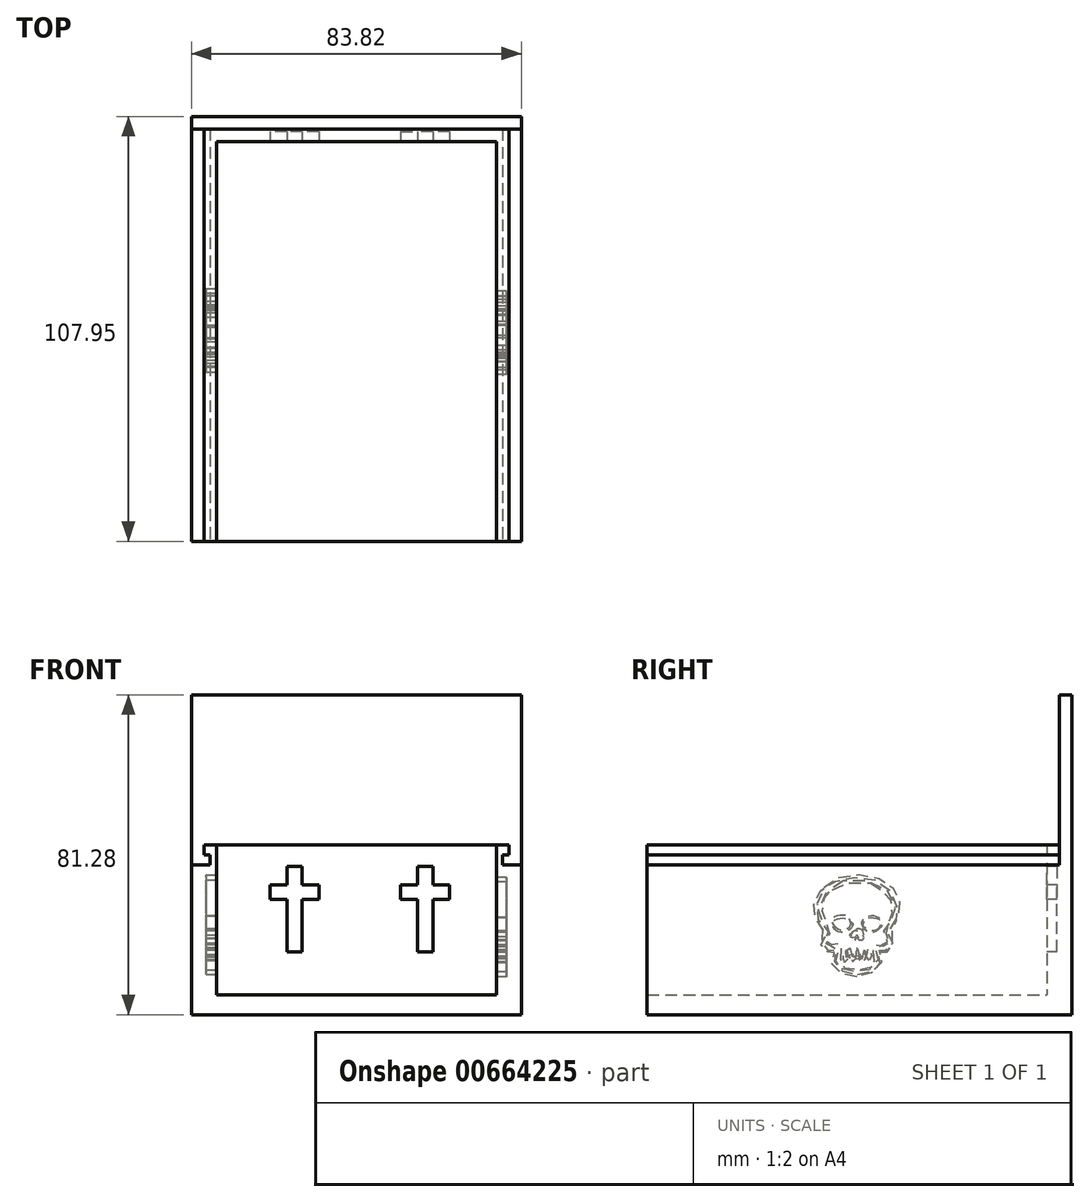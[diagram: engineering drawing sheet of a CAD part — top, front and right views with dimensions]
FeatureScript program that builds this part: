
annotation { "Feature Type Name" : "Feature", "Feature Type Description" : "" }
export const myFeature = defineFeature(function(context is Context, id is Id, definition is map)
    precondition{}
    {
        {
            var Q0;
            Q0=qCreatedBy(makeId("Top.planeOp"),FACE);
            var sketch = newSketch(context, id + "F0", { "sketchPlane" : qUnion([Q0])});
            skLineSegment(sketch, "E0.bottom", {"start": v(-35.56, 48.26) * mm, "end": v(35.56, 48.26) * mm});
            skLineSegment(sketch, "E0.top", {"start": v(-35.56, -48.26) * mm, "end": v(35.56, -48.26) * mm});
            skLineSegment(sketch, "E0.left", {"start": v(-35.56, 48.26) * mm, "end": v(-35.56, -48.26) * mm});
            skLineSegment(sketch, "E0.right", {"start": v(35.56, 48.26) * mm, "end": v(35.56, -48.26) * mm});
            skPoint(sketch, "E0.middle", {"position": v(0, 0) * mm});
            skLineSegment(sketch, "E1.bottom", {"start": v(-38.73, 51.44) * mm, "end": v(38.74, 51.44) * mm});
            skLineSegment(sketch, "E1.top", {"start": v(-38.74, -51.43) * mm, "end": v(38.73, -51.43) * mm});
            skLineSegment(sketch, "E1.left", {"start": v(-38.73, 51.44) * mm, "end": v(-38.74, -51.44) * mm});
            skLineSegment(sketch, "E1.right", {"start": v(38.74, 51.44) * mm, "end": v(38.73, -51.44) * mm});
            skLineSegment(sketch, "E2.bottom", {"start": v(-41.91, 54.61) * mm, "end": v(41.91, 54.61) * mm});
            skLineSegment(sketch, "E2.top", {"start": v(-41.91, -54.6) * mm, "end": v(41.91, -54.6) * mm});
            skLineSegment(sketch, "E2.left", {"start": v(-41.91, 54.61) * mm, "end": v(-41.91, -54.61) * mm});
            skLineSegment(sketch, "E2.right", {"start": v(41.91, 54.61) * mm, "end": v(41.91, -54.61) * mm});
            skLineSegment(sketch, "E3", {"start": v(-35.56, -48.26) * mm, "end": v(-41.91, -48.26) * mm});
            skLineSegment(sketch, "E4", {"start": v(35.56, -48.26) * mm, "end": v(41.91, -48.26) * mm});
            skSolve(sketch);
        }
        {
            var Q0;
            Q0=makeQuery(id+"F0.imprint","IMPRINT",FACE,{"disambiguationData":[TD([[makeQuery(id+"F0.imprint","IMPRINT",EDGE,{"derivedFrom":sQuery(id+"F0.wireOp",EDGE,"E1.bottom")}),1.0]])]});
            extrude(context, id + "F1", {"entities" : qUnion([Q0]), "depth" : 45.72 * mm, "offsetDistance" : 25.4 * mm});
        }
        {
            var Q0;
            Q0=makeQuery(id+"F0.imprint","IMPRINT",FACE,{"disambiguationData":[TD([[makeQuery(id+"F0.imprint","IMPRINT",EDGE,{"derivedFrom":sQuery(id+"F0.wireOp",EDGE,"E0.bottom")}),-1.0]])]});
            var Q1;
            Q1=makeQuery(id+"F0.imprint","IMPRINT",FACE,{"disambiguationData":[TD([[makeQuery(id+"F0.imprint","IMPRINT",EDGE,{"derivedFrom":sQuery(id+"F0.wireOp",EDGE,"E0.bottom")}),1.0]])]});
            extrude(context, id + "F2", {"entities" : qUnion([Q0, Q1]), "operationType" : NewBodyOperationType.ADD, "depth" : 12.7 * mm, "offsetDistance" : 25.4 * mm});
        }
        {
            var Q0;
            Q0=makeQuery(id+"F0.imprint","IMPRINT",FACE,{"disambiguationData":[TD([[makeQuery(id+"F0.imprint","IMPRINT",EDGE,{"derivedFrom":sQuery(id+"F0.wireOp",EDGE,"E0.bottom")}),1.0]])]});
            extrude(context, id + "F3", {"entities" : qUnion([Q0]), "operationType" : NewBodyOperationType.ADD, "depth" : 50.8 * mm, "offsetDistance" : 25.4 * mm});
        }
        {
            var Q0;
            Q0=makeQuery(id+"F3.opExtrude","SWEPT_FACE",FACE,{"disambiguationData":[OSD([sQuery(id+"F0.wireOp",EDGE,"E0.bottom")])]});
            var sketch = newSketch(context, id + "F4", { "sketchPlane" : qUnion([Q0])});
            skLineSegment(sketch, "E5", {"start": v(-21.92, 40.58) * mm, "end": v(-9.48, 40.58) * mm});
            skLineSegment(sketch, "E6", {"start": v(-9.48, 40.58) * mm, "end": v(-9.48, 36.95) * mm});
            skLineSegment(sketch, "E7", {"start": v(-9.48, 36.95) * mm, "end": v(-21.92, 36.95) * mm});
            skLineSegment(sketch, "E8", {"start": v(-21.92, 36.95) * mm, "end": v(-21.92, 40.58) * mm});
            skLineSegment(sketch, "E9", {"start": v(-15.7, 36.95) * mm, "end": v(-15.7, 24.23) * mm});
            skLineSegment(sketch, "E10", {"start": v(-15.7, 45.25) * mm, "end": v(-17.6, 45.25) * mm});
            skLineSegment(sketch, "E11", {"start": v(-17.6, 45.25) * mm, "end": v(-13.73, 45.25) * mm});
            skLineSegment(sketch, "E12", {"start": v(-13.73, 45.25) * mm, "end": v(-13.73, 23.57) * mm});
            skLineSegment(sketch, "E13", {"start": v(-13.73, 23.57) * mm, "end": v(-17.6, 23.57) * mm});
            skLineSegment(sketch, "E14", {"start": v(-17.6, 23.57) * mm, "end": v(-17.6, 45.25) * mm});
            skLineSegment(sketch, "E15", {"start": v(11.25, 40.6) * mm, "end": v(23.7, 40.6) * mm});
            skLineSegment(sketch, "E16", {"start": v(23.7, 40.6) * mm, "end": v(23.7, 36.97) * mm});
            skLineSegment(sketch, "E17", {"start": v(23.7, 36.97) * mm, "end": v(11.25, 36.97) * mm});
            skLineSegment(sketch, "E18", {"start": v(11.25, 36.97) * mm, "end": v(11.25, 40.6) * mm});
            skLineSegment(sketch, "E19", {"start": v(15.58, 45.26) * mm, "end": v(19.44, 45.26) * mm});
            skLineSegment(sketch, "E20", {"start": v(19.44, 45.26) * mm, "end": v(19.44, 23.59) * mm});
            skLineSegment(sketch, "E21", {"start": v(19.44, 23.59) * mm, "end": v(15.58, 23.59) * mm});
            skLineSegment(sketch, "E22", {"start": v(15.58, 23.59) * mm, "end": v(15.58, 45.26) * mm});
            skSolve(sketch);
        }
        {
            var Q0;
            Q0 = qSketchRegion(id + "F4", true);
            extrude(context, id + "F5", {"entities" : qUnion([Q0]), "operationType" : NewBodyOperationType.REMOVE, "oppositeDirection" : true, "depth" : 2.54 * mm, "offsetDistance" : 25.4 * mm});
        }
        {
            var Q0;
            Q0=makeQuery(id+"F3.opExtrude","SWEPT_FACE",FACE,{"disambiguationData":[OSD([sQuery(id+"F0.wireOp",EDGE,"E0.left")])]});
            var sketch = newSketch(context, id + "F6", { "sketchPlane" : qUnion([Q0])});
            skFitSpline(sketch, "E23", {"points": [v(-3.48, 41.6) * mm, v(-6.98, 39.1) * mm, v(-8.94, 36.07) * mm, v(-8.17, 31.6) * mm, v(-7.36, 29.82) * mm, v(-7.6, 27.83) * mm, v(-8.05, 26.07) * mm, v(-6.59, 25.46) * mm, v(-5.74, 25.8) * mm, v(-4.17, 25.42) * mm, v(-4.08, 24.6) * mm, v(-4.26, 22.37) * mm, v(-3.84, 20.01) * mm, v(0.07, 19.06) * mm, v(4.06, 20) * mm, v(5.35, 21.75) * mm, v(4.77, 24.34) * mm, v(6.05, 25.5) * mm, v(7.42, 25.48) * mm, v(7.65, 26.53) * mm, v(6.85, 29.25) * mm, v(9.08, 31.8) * mm, v(7.97, 38.98) * mm, v(-3.48, 41.6) * mm]});
            skFitSpline(sketch, "E24", {"points": [v(-1.81, 24.6) * mm, v(-1.36, 22.37) * mm, v(-0.58, 24.16) * mm, v(-0.04, 24.6) * mm, v(0.17, 23.93) * mm, v(0.54, 22.37) * mm, v(1.28, 24.13) * mm, v(2.4, 22.37) * mm, v(2.88, 24.6) * mm, v(3.56, 22.91) * mm, v(2.96, 21.49) * mm, v(1.62, 23) * mm, v(1.02, 21.62) * mm, v(-0.16, 22.82) * mm, v(-1.1, 21.45) * mm, v(-2.57, 23.8) * mm, v(-1.81, 24.6) * mm]});
            skFitSpline(sketch, "E25", {"points": [v(-2.96, 32.8) * mm, v(-6.4, 31.85) * mm, v(-4.26, 29.17) * mm, v(-1.81, 30.11) * mm, v(-1.81, 31.7) * mm, v(-2.96, 32.8) * mm]});
            skFitSpline(sketch, "E26", {"points": [v(1.64, 31.89) * mm, v(1.1, 30.65) * mm, v(3.98, 29.03) * mm, v(5.86, 30.16) * mm, v(5.89, 31.9) * mm, v(3.37, 32.7) * mm, v(1.64, 31.89) * mm]});
            skFitSpline(sketch, "E27", {"points": [v(-0.04, 27.93) * mm, v(-0.58, 27.28) * mm, v(-1.81, 27.7) * mm, v(0.54, 29.52) * mm, v(1.5, 27.57) * mm, v(0.54, 27.08) * mm, v(-0.04, 27.93) * mm]});
            skPoint(sketch, "E28.18.internal.snap0", {"position": v(-8.94, 30.33) * mm});
            skFitSpline(sketch, "E28", {"points": [v(0.07, 17.85) * mm, v(4.62, 19.06) * mm, v(6.3, 21.62) * mm, v(5.67, 23.93) * mm, v(6.14, 24.16) * mm, v(7.54, 24.16) * mm, v(9.08, 25.48) * mm, v(8.3, 27.85) * mm, v(7.65, 28.63) * mm, v(9.08, 30.33) * mm, v(10.57, 33.02) * mm, v(10.74, 36.88) * mm, v(7.97, 40.84) * mm, v(1.02, 43.07) * mm, v(-6.4, 41.6) * mm, v(-9.91, 36.93) * mm, v(-9.9, 31.85) * mm, v(-8.94, 30.33) * mm, v(-8.94, 26.53) * mm, v(-8.15, 24.16) * mm, v(-6.4, 24.16) * mm, v(-5.28, 23.93) * mm, v(-5.8, 21.62) * mm, v(-4.26, 19.06) * mm, v(0.07, 17.85) * mm]});
            skPoint(sketch, "E29.18.internal.snap0", {"position": v(-5.14, 42.6) * mm});
            skSolve(sketch);
        }
        {
            var Q0;
            Q0 = qSketchRegion(id + "F6", true);
            var Q1;
            Q1=makeQuery(id+"F6.imprint","IMPRINT",FACE,{"disambiguationData":[TD([[makeQuery(id+"F6.imprint","IMPRINT",EDGE,{"derivedFrom":sQuery(id+"F6.wireOp",EDGE,"E25")}),1.0]])]});
            var Q2;
            Q2=makeQuery(id+"F6.imprint","IMPRINT",FACE,{"disambiguationData":[TD([[makeQuery(id+"F6.imprint","IMPRINT",EDGE,{"derivedFrom":sQuery(id+"F6.wireOp",EDGE,"E27")}),-1.0]])]});
            var Q3;
            Q3=makeQuery(id+"F6.imprint","IMPRINT",FACE,{"disambiguationData":[TD([[makeQuery(id+"F6.imprint","IMPRINT",EDGE,{"derivedFrom":sQuery(id+"F6.wireOp",EDGE,"E26")}),1.0]])]});
            var Q4;
            Q4=makeQuery(id+"F6.imprint","IMPRINT",FACE,{"disambiguationData":[TD([[makeQuery(id+"F6.imprint","IMPRINT",EDGE,{"derivedFrom":sQuery(id+"F6.wireOp",EDGE,"E24")}),-1.0]])]});
            extrude(context, id + "F7", {"entities" : qUnion([Q0, Q1, Q2, Q3, Q4]), "operationType" : NewBodyOperationType.REMOVE, "oppositeDirection" : true, "depth" : 2.54 * mm, "offsetDistance" : 25.4 * mm});
        }
        {
            var Q0;
            Q0=makeQuery(id+"F3.opExtrude","SWEPT_FACE",FACE,{"disambiguationData":[OSD([sQuery(id+"F0.wireOp",EDGE,"E1.left")])]});
            var sketch = newSketch(context, id + "F8", { "sketchPlane" : qUnion([Q0])});
            skLineSegment(sketch, "E30.bottom", {"start": v(-51.43, 45.72) * mm, "end": v(48.26, 45.72) * mm});
            skLineSegment(sketch, "E30.top", {"start": v(-51.43, 48.26) * mm, "end": v(48.26, 48.26) * mm});
            skLineSegment(sketch, "E30.left", {"start": v(-51.43, 45.72) * mm, "end": v(-51.43, 48.26) * mm});
            skLineSegment(sketch, "E30.right", {"start": v(48.26, 45.72) * mm, "end": v(48.26, 48.26) * mm});
            skSolve(sketch);
        }
        {
            var Q0;
            Q0 = qSketchRegion(id + "F8", true);
            extrude(context, id + "F9", {"entities" : qUnion([Q0]), "operationType" : NewBodyOperationType.REMOVE, "depth" : -1.57 * mm, "offsetDistance" : 25.4 * mm});
        }
        {
            var Q0;
            Q0=makeQuery(id+"F3.opExtrude","SWEPT_FACE",FACE,{"disambiguationData":[OSD([sQuery(id+"F0.wireOp",EDGE,"E1.right")])]});
            var sketch = newSketch(context, id + "F10", { "sketchPlane" : qUnion([Q0])});
            skLineSegment(sketch, "E31.bottom", {"start": v(-48.26, 45.72) * mm, "end": v(51.44, 45.72) * mm});
            skLineSegment(sketch, "E31.top", {"start": v(-48.26, 48.26) * mm, "end": v(51.44, 48.26) * mm});
            skLineSegment(sketch, "E31.left", {"start": v(-48.26, 45.72) * mm, "end": v(-48.26, 48.26) * mm});
            skLineSegment(sketch, "E31.right", {"start": v(51.44, 45.72) * mm, "end": v(51.44, 48.26) * mm});
            skSolve(sketch);
        }
        {
            var Q0;
            Q0 = qSketchRegion(id + "F10", true);
            extrude(context, id + "F11", {"entities" : qUnion([Q0]), "operationType" : NewBodyOperationType.REMOVE, "depth" : -1.57 * mm, "offsetDistance" : 25.4 * mm});
        }
        {
            var Q0;
            {var subQ0=sQuery(id+"F0.wireOp",EDGE,"E4");var subQ1=sQuery(id+"F0.wireOp",EDGE,"E3");var subQ2=sQuery(id+"F0.wireOp",EDGE,"E1.right");var subQ3=sQuery(id+"F0.wireOp",EDGE,"E1.left");var subQ4=sQuery(id+"F0.wireOp",EDGE,"E1.bottom");Q0=makeQuery(id+"F2.boolean.opBoolean","MERGE",FACE,{"derivedFrom":[makeQuery(id+"F1.opExtrude","CAP_FACE",FACE,{"disambiguationData":[OSD([subQ4,subQ3,subQ2,sQuery(id+"F0.wireOp",EDGE,"E2.bottom"),sQuery(id+"F0.wireOp",EDGE,"E2.left"),sQuery(id+"F0.wireOp",EDGE,"E2.right"),subQ1,subQ0])],"isStart":true}),makeQuery(id+"F2.opExtrude","CAP_FACE",FACE,{"disambiguationData":[OSD([sQuery(id+"F0.wireOp",EDGE,"E0.top"),subQ4,subQ3,subQ2,subQ1,subQ0])],"isStart":true})]});}
            var sketch = newSketch(context, id + "F12", { "sketchPlane" : qUnion([Q0])});
            skLineSegment(sketch, "E32.bottom", {"start": v(-41.91, 48.26) * mm, "end": v(41.91, 48.26) * mm});
            skLineSegment(sketch, "E32.top", {"start": v(-41.91, -54.61) * mm, "end": v(41.91, -54.61) * mm});
            skLineSegment(sketch, "E32.left", {"start": v(-41.91, 48.26) * mm, "end": v(-41.91, -54.61) * mm});
            skLineSegment(sketch, "E32.right", {"start": v(41.91, 48.26) * mm, "end": v(41.91, -54.61) * mm});
            skSolve(sketch);
        }
        {
            var Q0;
            Q0 = qSketchRegion(id + "F12", true);
            extrude(context, id + "F13", {"entities" : qUnion([Q0]), "operationType" : NewBodyOperationType.REMOVE, "oppositeDirection" : true, "depth" : 7.62 * mm, "offsetDistance" : 25.4 * mm});
        }
        {
            var Q0;
            Q0=makeQuery(id+"F11.boolean.opBoolean","MERGE",FACE,{"derivedFrom":[makeQuery(id+"F9.boolean.opBoolean","MERGE",FACE,{"derivedFrom":[makeQuery(id+"F1.opExtrude","CAP_FACE",FACE,{"disambiguationData":[OSD([sQuery(id+"F0.wireOp",EDGE,"E1.bottom"),sQuery(id+"F0.wireOp",EDGE,"E1.left"),sQuery(id+"F0.wireOp",EDGE,"E1.right"),sQuery(id+"F0.wireOp",EDGE,"E2.bottom"),sQuery(id+"F0.wireOp",EDGE,"E2.left"),sQuery(id+"F0.wireOp",EDGE,"E2.right"),sQuery(id+"F0.wireOp",EDGE,"E3"),sQuery(id+"F0.wireOp",EDGE,"E4")])],"isStart":false}),makeQuery(id+"F9.opExtrude","SWEPT_FACE",FACE,{"disambiguationData":[OSD([sQuery(id+"F8.wireOp",EDGE,"E30.bottom")])]})]}),makeQuery(id+"F11.opExtrude","SWEPT_FACE",FACE,{"disambiguationData":[OSD([sQuery(id+"F10.wireOp",EDGE,"E31.bottom")])]})]});
            var sketch = newSketch(context, id + "F14", { "sketchPlane" : qUnion([Q0])});
            skLineSegment(sketch, "E33.bottom", {"start": v(-41.91, 54.61) * mm, "end": v(41.91, 54.61) * mm});
            skLineSegment(sketch, "E33.top", {"start": v(-41.91, 51.44) * mm, "end": v(41.91, 51.44) * mm});
            skLineSegment(sketch, "E33.left", {"start": v(-41.91, 54.61) * mm, "end": v(-41.91, 51.44) * mm});
            skLineSegment(sketch, "E33.right", {"start": v(41.91, 54.61) * mm, "end": v(41.91, 51.44) * mm});
            skSolve(sketch);
        }
        {
            var Q0;
            Q0 = qSketchRegion(id + "F14", true);
            extrude(context, id + "F15", {"entities" : qUnion([Q0]), "operationType" : NewBodyOperationType.ADD, "depth" : 43.18 * mm, "offsetDistance" : 25.4 * mm});
        }
        {
            var Q0;
            Q0=makeQuery(id+"F3.opExtrude","SWEPT_FACE",FACE,{"disambiguationData":[OSD([sQuery(id+"F0.wireOp",EDGE,"E0.right")])]});
            var sketch = newSketch(context, id + "F16", { "sketchPlane" : qUnion([Q0])});
            skFitSpline(sketch, "E34", {"points": [v(-3.42, 41.06) * mm, v(-6.93, 38.57) * mm, v(-8.89, 35.54) * mm, v(-8.11, 31.06) * mm, v(-7.3, 29.29) * mm, v(-7.55, 27.3) * mm, v(-8, 25.54) * mm, v(-6.54, 24.93) * mm, v(-5.69, 25.27) * mm, v(-4.11, 24.9) * mm, v(-4.02, 24.07) * mm, v(-4.2, 21.84) * mm, v(-3.79, 19.48) * mm, v(0.12, 18.53) * mm, v(4.11, 19.47) * mm, v(5.4, 21.22) * mm, v(4.82, 23.81) * mm, v(6.1, 24.97) * mm, v(7.47, 24.94) * mm, v(7.7, 26) * mm, v(6.9, 28.71) * mm, v(9.13, 31.27) * mm, v(8.02, 38.45) * mm, v(-3.42, 41.06) * mm]});
            skFitSpline(sketch, "E35", {"points": [v(-1.7, 24.07) * mm, v(-1.25, 21.84) * mm, v(-0.47, 23.57) * mm, v(0.06, 24.07) * mm, v(0.27, 23.33) * mm, v(0.65, 21.84) * mm, v(1.4, 23.54) * mm, v(2.51, 21.84) * mm, v(3, 24.07) * mm, v(3.67, 22.32) * mm, v(3.07, 20.9) * mm, v(1.73, 22.4) * mm, v(1.13, 21.02) * mm, v(-0.05, 22.23) * mm, v(-1, 20.86) * mm, v(-2.47, 23.2) * mm, v(-1.7, 24.07) * mm]});
            skFitSpline(sketch, "E36", {"points": [v(-2.85, 32.2) * mm, v(-6.3, 31.25) * mm, v(-4.2, 28.57) * mm, v(-1.7, 29.51) * mm, v(-1.7, 31.1) * mm, v(-2.85, 32.2) * mm]});
            skFitSpline(sketch, "E37", {"points": [v(1.7, 31.36) * mm, v(1.15, 30.12) * mm, v(4.03, 28.5) * mm, v(5.9, 29.63) * mm, v(5.94, 31.37) * mm, v(3.42, 32.16) * mm, v(1.7, 31.36) * mm]});
            skFitSpline(sketch, "E38", {"points": [v(0.06, 27.33) * mm, v(-0.47, 26.68) * mm, v(-1.7, 27.1) * mm, v(0.65, 28.93) * mm, v(1.6, 26.97) * mm, v(0.65, 26.48) * mm, v(0.06, 27.33) * mm]});
            skPoint(sketch, "E39.18.internal.snap0", {"position": v(-8.89, 29.8) * mm});
            skFitSpline(sketch, "E39", {"points": [v(0.12, 17.25) * mm, v(4.73, 18.53) * mm, v(6.4, 21.02) * mm, v(5.77, 23.33) * mm, v(6.25, 23.57) * mm, v(7.65, 23.57) * mm, v(9.13, 24.94) * mm, v(8.4, 27.25) * mm, v(7.7, 28.03) * mm, v(9.13, 29.8) * mm, v(10.68, 32.42) * mm, v(10.85, 36.29) * mm, v(8.02, 40.24) * mm, v(1.13, 42.47) * mm, v(-6.3, 41.06) * mm, v(-9.8, 36.33) * mm, v(-9.8, 31.25) * mm, v(-8.89, 29.8) * mm, v(-8.89, 26) * mm, v(-8.04, 23.57) * mm, v(-6.3, 23.57) * mm, v(-5.17, 23.33) * mm, v(-5.69, 21.02) * mm, v(-4.2, 18.53) * mm, v(0.12, 17.25) * mm]});
            skSolve(sketch);
        }
        {
            var Q0;
            Q0=makeQuery(id+"F16.imprint","IMPRINT",FACE,{"disambiguationData":[TD([[makeQuery(id+"F16.imprint","IMPRINT",EDGE,{"derivedFrom":sQuery(id+"F16.wireOp",EDGE,"E36")}),1.0]])]});
            var Q1;
            Q1=makeQuery(id+"F16.imprint","IMPRINT",FACE,{"disambiguationData":[TD([[makeQuery(id+"F16.imprint","IMPRINT",EDGE,{"derivedFrom":sQuery(id+"F16.wireOp",EDGE,"E37")}),1.0]])]});
            var Q2;
            Q2=makeQuery(id+"F16.imprint","IMPRINT",FACE,{"disambiguationData":[TD([[makeQuery(id+"F16.imprint","IMPRINT",EDGE,{"derivedFrom":sQuery(id+"F16.wireOp",EDGE,"E35")}),-1.0]])]});
            var Q3;
            Q3=makeQuery(id+"F16.imprint","IMPRINT",FACE,{"disambiguationData":[TD([[makeQuery(id+"F16.imprint","IMPRINT",EDGE,{"derivedFrom":sQuery(id+"F16.wireOp",EDGE,"E38")}),-1.0]])]});
            var Q4;
            Q4=makeQuery(id+"F16.imprint","IMPRINT",FACE,{"disambiguationData":[TD([[makeQuery(id+"F16.imprint","IMPRINT",EDGE,{"derivedFrom":sQuery(id+"F16.wireOp",EDGE,"E34")}),-1.0]])]});
            extrude(context, id + "F17", {"entities" : qUnion([Q0, Q1, Q2, Q3, Q4]), "operationType" : NewBodyOperationType.REMOVE, "oppositeDirection" : true, "depth" : 2.54 * mm, "offsetDistance" : 25.4 * mm});
        }
        {
            var Q0;
            {var subQ0=sQuery(id+"F0.wireOp",EDGE,"E4");var subQ1=sQuery(id+"F0.wireOp",EDGE,"E3");Q0=makeQuery(id+"F3.boolean.opBoolean","MERGE",FACE,{"derivedFrom":[makeQuery(id+"F2.boolean.opBoolean","MERGE",FACE,{"derivedFrom":[makeQuery(id+"F1.opExtrude","SWEPT_FACE",FACE,{"disambiguationData":[OSD([subQ1])]}),makeQuery(id+"F1.opExtrude","SWEPT_FACE",FACE,{"disambiguationData":[OSD([subQ0])]}),makeQuery(id+"F2.opExtrude","SWEPT_FACE",FACE,{"disambiguationData":[OSD([sQuery(id+"F0.wireOp",EDGE,"E0.top"),subQ1,subQ0])]})]}),makeQuery(id+"F3.opExtrude","SWEPT_FACE",FACE,{"disambiguationData":[OSD([subQ1])]}),makeQuery(id+"F3.opExtrude","SWEPT_FACE",FACE,{"disambiguationData":[OSD([subQ0])]})]});}
            var sketch = newSketch(context, id + "F18", { "sketchPlane" : qUnion([Q0])});
            skLineSegment(sketch, "E40", {"start": v(-38.74, 50.8) * mm, "end": v(-35.56, 50.8) * mm});
            skLineSegment(sketch, "E41", {"start": v(-35.56, 50.8) * mm, "end": v(-35.56, 12.7) * mm});
            skLineSegment(sketch, "E42", {"start": v(-35.56, 12.7) * mm, "end": v(35.56, 12.7) * mm});
            skLineSegment(sketch, "E43", {"start": v(35.56, 12.7) * mm, "end": v(35.56, 50.8) * mm});
            skLineSegment(sketch, "E44", {"start": v(35.56, 50.8) * mm, "end": v(38.74, 50.8) * mm});
            skLineSegment(sketch, "E45", {"start": v(38.74, 50.8) * mm, "end": v(38.74, 48.26) * mm});
            skLineSegment(sketch, "E46", {"start": v(38.74, 48.26) * mm, "end": v(37.16, 48.26) * mm});
            skLineSegment(sketch, "E47", {"start": v(37.16, 48.26) * mm, "end": v(37.16, 45.72) * mm});
            skLineSegment(sketch, "E48", {"start": v(37.16, 45.72) * mm, "end": v(41.91, 45.72) * mm});
            skLineSegment(sketch, "E49", {"start": v(41.91, 45.72) * mm, "end": v(41.91, 7.62) * mm});
            skLineSegment(sketch, "E50", {"start": v(41.91, 7.62) * mm, "end": v(-41.91, 7.62) * mm});
            skLineSegment(sketch, "E51", {"start": v(-41.91, 7.62) * mm, "end": v(-41.91, 45.72) * mm});
            skLineSegment(sketch, "E52", {"start": v(-41.91, 45.72) * mm, "end": v(-37.16, 45.72) * mm});
            skLineSegment(sketch, "E53", {"start": v(-37.16, 45.72) * mm, "end": v(-37.16, 48.26) * mm});
            skLineSegment(sketch, "E54", {"start": v(-37.16, 48.26) * mm, "end": v(-38.74, 48.26) * mm});
            skLineSegment(sketch, "E55", {"start": v(-38.74, 48.26) * mm, "end": v(-38.74, 50.8) * mm});
            skSolve(sketch);
        }
        {
            var Q0;
            Q0 = qSketchRegion(id + "F18", true);
            extrude(context, id + "F19", {"entities" : qUnion([Q0]), "operationType" : NewBodyOperationType.ADD, "depth" : 5.08 * mm, "offsetDistance" : 25.4 * mm});
        }
    });
